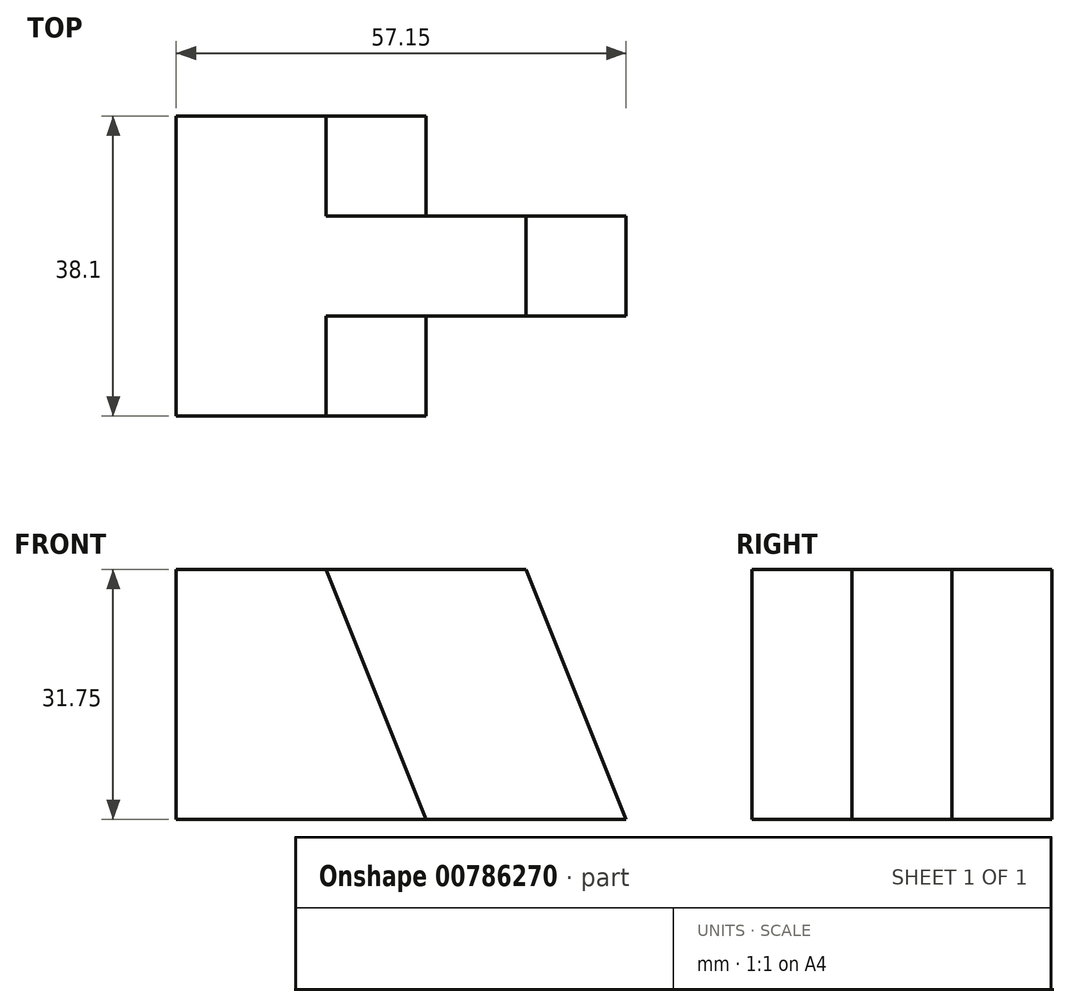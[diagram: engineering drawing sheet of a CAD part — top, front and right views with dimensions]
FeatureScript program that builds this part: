
annotation { "Feature Type Name" : "Feature", "Feature Type Description" : "" }
export const myFeature = defineFeature(function(context is Context, id is Id, definition is map)
    precondition{}
    {
        {
            var Q0;
            Q0=qCreatedBy(makeId("Front.planeOp"),FACE);
            var sketch = newSketch(context, id + "F0", { "sketchPlane" : qUnion([Q0])});
            skLineSegment(sketch, "E0", {"start": v(0, 0) * mm, "end": v(57.15, 0) * mm});
            skLineSegment(sketch, "E1", {"start": v(57.15, 0) * mm, "end": v(57.15, 31.75) * mm});
            skLineSegment(sketch, "E2", {"start": v(57.15, 31.75) * mm, "end": v(0, 31.75) * mm});
            skLineSegment(sketch, "E3", {"start": v(0, 31.75) * mm, "end": v(0, 0) * mm});
            skSolve(sketch);
        }
        {
            var Q0;
            Q0 = qSketchRegion(id + "F0", true);
            extrude(context, id + "F1", {"entities" : qUnion([Q0]), "depth" : 38.1 * mm, "offsetDistance" : 25.4 * mm});
        }
        {
            var Q0;
            Q0=makeQuery(id+"F1.opExtrude","CAP_FACE",FACE,{"disambiguationData":[OSD([sQuery(id+"F0.wireOp",EDGE,"E0"),sQuery(id+"F0.wireOp",EDGE,"E1"),sQuery(id+"F0.wireOp",EDGE,"E2"),sQuery(id+"F0.wireOp",EDGE,"E3")])],"isStart":false});
            var sketch = newSketch(context, id + "F2", { "sketchPlane" : qUnion([Q0])});
            skLineSegment(sketch, "E4", {"start": v(0, 31.75) * mm, "end": v(19.05, 31.75) * mm});
            skLineSegment(sketch, "E5", {"start": v(0, 0) * mm, "end": v(31.75, 0) * mm});
            skLineSegment(sketch, "E6", {"start": v(19.05, 31.75) * mm, "end": v(31.75, 0) * mm});
            skSolve(sketch);
        }
        {
            var Q0;
            {var subQ0=sQuery(id+"F2.wireOp",EDGE,"E6");Q0=makeQuery(id+"F2.imprint","IMPRINT",FACE,{"disambiguationData":[TD([[makeQuery(id+"F2.imprint","IMPRINT",EDGE,{"derivedFrom":subQ0}),1.0]])]});}
            extrude(context, id + "F3", {"entities" : qUnion([Q0]), "operationType" : NewBodyOperationType.REMOVE, "oppositeDirection" : true, "depth" : 12.7 * mm, "offsetDistance" : 25.4 * mm});
        }
        {
            var Q0;
            Q0=makeQuery(id+"F1.opExtrude","CAP_FACE",FACE,{"disambiguationData":[OSD([sQuery(id+"F0.wireOp",EDGE,"E0"),sQuery(id+"F0.wireOp",EDGE,"E1"),sQuery(id+"F0.wireOp",EDGE,"E2"),sQuery(id+"F0.wireOp",EDGE,"E3")])],"isStart":true});
            var sketch = newSketch(context, id + "F4", { "sketchPlane" : qUnion([Q0])});
            skLineSegment(sketch, "E7", {"start": v(0, 31.75) * mm, "end": v(-19.05, 31.75) * mm});
            skLineSegment(sketch, "E8", {"start": v(0, 0) * mm, "end": v(-31.75, 0) * mm});
            skLineSegment(sketch, "E9", {"start": v(-19.05, 31.75) * mm, "end": v(-31.75, 0) * mm});
            skSolve(sketch);
        }
        {
            var Q0;
            {var subQ0=sQuery(id+"F4.wireOp",EDGE,"E9");Q0=makeQuery(id+"F4.imprint","IMPRINT",FACE,{"disambiguationData":[TD([[makeQuery(id+"F4.imprint","IMPRINT",EDGE,{"derivedFrom":subQ0}),-1.0]])]});}
            extrude(context, id + "F5", {"entities" : qUnion([Q0]), "operationType" : NewBodyOperationType.REMOVE, "oppositeDirection" : true, "depth" : 12.7 * mm, "offsetDistance" : 25.4 * mm});
        }
        {
            var Q0;
            Q0=makeQuery(id+"F3.boolean.opBoolean","COPY",FACE,{"derivedFrom":makeQuery(id+"F3.opExtrude","CAP_FACE",FACE,{"disambiguationData":[OSD([sQuery(id+"F0.wireOp",EDGE,"E0"),sQuery(id+"F0.wireOp",EDGE,"E1"),sQuery(id+"F0.wireOp",EDGE,"E2"),sQuery(id+"F2.wireOp",EDGE,"E6")])],"isStart":false})});
            var sketch = newSketch(context, id + "F6", { "sketchPlane" : qUnion([Q0])});
            skLineSegment(sketch, "E10", {"start": v(19.05, 31.75) * mm, "end": v(44.45, 31.75) * mm});
            skLineSegment(sketch, "E11", {"start": v(44.45, 31.75) * mm, "end": v(57.15, 0) * mm});
            skSolve(sketch);
        }
        {
            var Q0;
            {var subQ0=sQuery(id+"F6.wireOp",EDGE,"E11");Q0=makeQuery(id+"F6.imprint","IMPRINT",FACE,{"disambiguationData":[TD([[makeQuery(id+"F6.imprint","IMPRINT",EDGE,{"derivedFrom":subQ0}),1.0]])]});}
            extrude(context, id + "F7", {"entities" : qUnion([Q0]), "operationType" : NewBodyOperationType.REMOVE, "oppositeDirection" : true, "depth" : 12.7 * mm, "offsetDistance" : 25.4 * mm});
        }
    });
